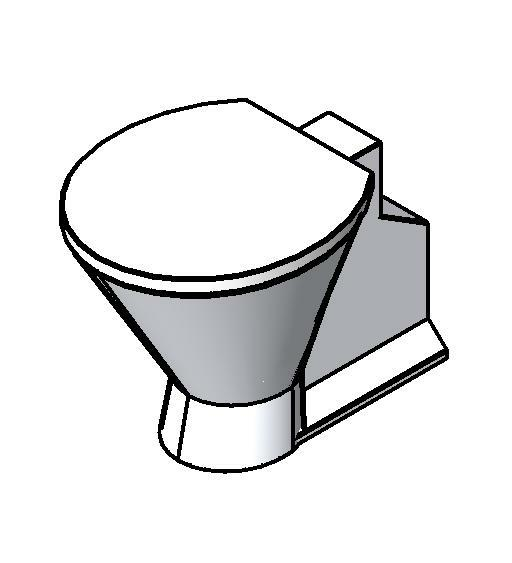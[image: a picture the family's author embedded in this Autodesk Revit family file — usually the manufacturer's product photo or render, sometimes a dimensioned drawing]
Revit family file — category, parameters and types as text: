
# Revit family: Deca_Bica para lavatório mesa wave baixa_Deca You_1790.106
name_source: partatom
category: Plumbing Fixtures
units: mm (PartAtom-declared; Revit-internal decimal feet)

## family parameters
Cut with Voids When Loaded = No
Host = Face
Part Type = Normal
Room Calculation Point = No
Round Connector Dimension = Use Radius
Shared = No

## types (10) — shared parameters
Acompanha o Produto = Restritor de Vazão Deca Comfort
Aprovado por = quattroD
Atendimento ao Cliente = 0800-0117073
Categoria = Bica Lavatório / Banheiro
Composição Básica = Liga de Cobre (Latão),Plásticos de Engenharia e Elastômeros
Consumo = -
Cor Secundária = -
Criado por = quattroD
Itens de Instalação = Mangeira Flexivel
Linha = Deca You
Manufacturer = DECA
Norma = Não possui
Pressão mín. Aquec. Acúmulo = -
Pressão mín. Aquec. Passagem = -
Saída de Esgoto = -
Segmento = Luxo
Tipo de dispositivo economizador = Decacomfort
Tipo de mecanismo utilizado = Não Possui
Tipo de rosca de entrada = BSP
Tipo de rosca de saída = -
URL = www.deca.com.br
zero-valued in all types: CWFU, Default Elevation, Diâmetro Ponto de Esgoto, Diâmetro Água Fria, Peso Líquido (Kg), Raio Ponto de Esgoto, Raio Água Fria, WFU

## per-type parameters (varying)
| type | Cor Principal | Código Pai | Material | Model |
| 1790.BL106.MT_Black Matte | Black Matte | 1790.BL106.MT | Deca_Black Matte | 1790.BL106.MT |
| 1790.GF106.MT_Antracite | Antracite Dark | 1790.GF106.MT | Deca_Antracite | 1790.GF106.MT |
| 1790.INX106_Inox | Inox | 1790.INX106 | Deca_Inox | 1790.INX106 |
| 1790.SM106.MT_Summer Gold | SUMMER GOLD | 1790.SM106.MT | Deca_Summer Gold | 1790.SM106.MT |
| 1790.MR106.MT_Brown Matte | Dynamic Brown | 1790.MR106.MT | Deca_Brown Matte | 1790.MR106.MT |
| 1790.LS106.MT_Dynamic Gold | Dynamic Gold | 1790.LS106.MT | Deca_Dynamic Gold | 1790.LS106.MT |
| 1790.CL106.MT_Dynamic Peach | Dynamic Peach | 1790.CL106.MT | Deca_Dynamic Peach | 1790.CL106.MT |
| 1790.AZ106.MT_Dynamic Blue | Dynamic Blue | 1790.AZ106.MT | Deca_Dynamic Blue | 1790.AZ106.MT |
| 1790.BR106.MT_ Dynamic White | Dynamic White | 1790.BR106.MT | Deca_Dynamic White | 1790.BR106.MT |
| 1790.LV106.MT_Dynamic Lilac | Dynamic Lilac | 1790.LV106.MT | Deca_Dynamic Lilac | 1790.LV106.MT |

## geometry (parser evidence)
native form markers: Sweep x2
no freeform markers — native parametric forms only
